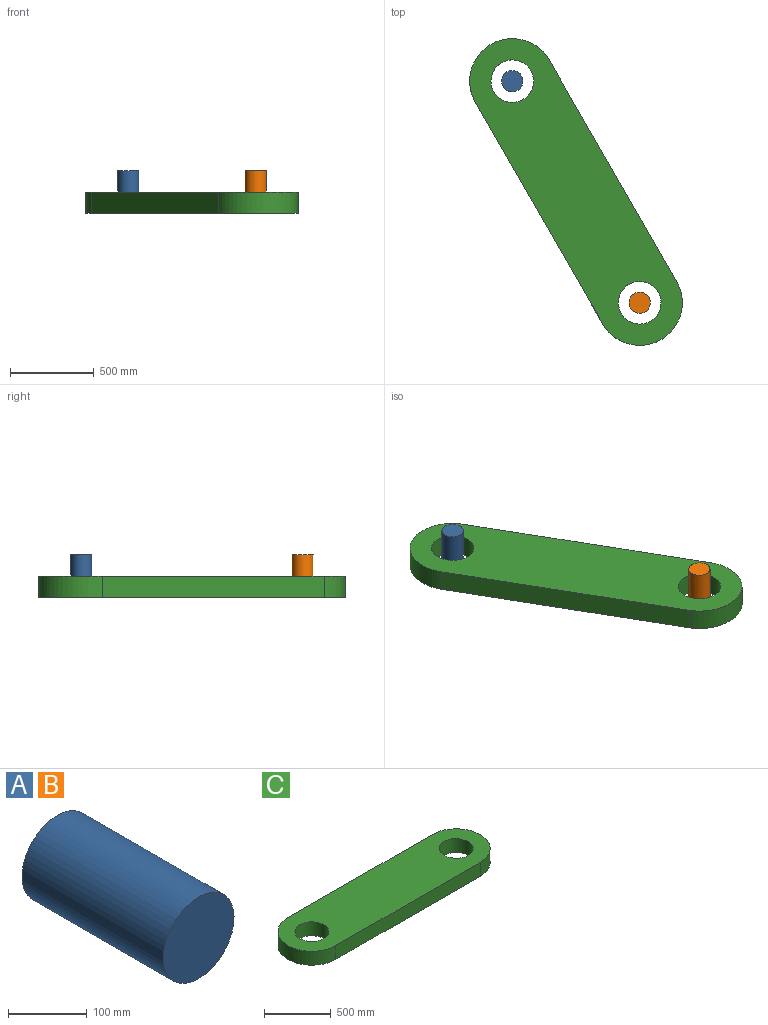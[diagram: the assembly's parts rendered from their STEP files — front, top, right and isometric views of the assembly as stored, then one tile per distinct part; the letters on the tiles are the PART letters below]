
ASSEMBLY  parts=3 mates=2
PART A: 3 faces, bbox 127x254x127 mm
  f0: cylinder r=63.5mm len=254mm, axis (0,1,0), area 101341.5mm2, adj f1,f2
  f1: plane 127x127mm, normal (0,-1,0), area 12667.7mm2, adj f0
  f2: plane 127x127mm, normal (0,1,0), area 12667.7mm2, adj f0
PART B: same geometry as A
PART C: 8 faces, bbox 2032x508x127 mm
  f0: plane 1524x127mm, normal (0,1,0), area 193548mm2, adj f1,f5,f6,f7
  f1: cylinder r=254mm len=508mm, axis (0,0,-1), area 101341.5mm2, adj f0,f2,f6,f7
  f2: plane 1524x127mm, normal (0,-1,0), area 193548mm2, adj f1,f5,f6,f7
  f3: cylinder r=127mm len=254mm, axis (0,0,-1), area 101341.5mm2, adj f6,f7
  f4: cylinder r=127mm len=254mm, axis (0,0,-1), area 101341.5mm2, adj f6,f7
  f5: cylinder r=254mm len=508mm, axis (0,0,-1), area 101341.5mm2, adj f0,f2,f6,f7
  f6: plane 2032x508mm, normal (0,0,1), area 875533.5mm2, adj f0,f1,f2,f3,f4,f5
  f7: plane 2032x508mm, normal (0,0,-1), area 875533.5mm2, adj f0,f1,f2,f3,f4,f5
PLACE A rot(axis=(0.94,0.25,0.25),93.8deg) t=(1230.43,1291.42,0)mm
PLACE B rot(axis=(1,0,0),90deg) t=(1990.43,-29.55,0)mm
PLACE C rot(axis=(0,0,-1),60.1deg) t=(1610.43,630.94,-127)mm
MATE cylindrical B.f0 <-> C.f3  axis (0,0,1) through (1990.43,-29.55,0)mm
MATE slider A.f0 <-> C.f4  axis (0,0,1) through (1230.43,1291.42,0)mm
